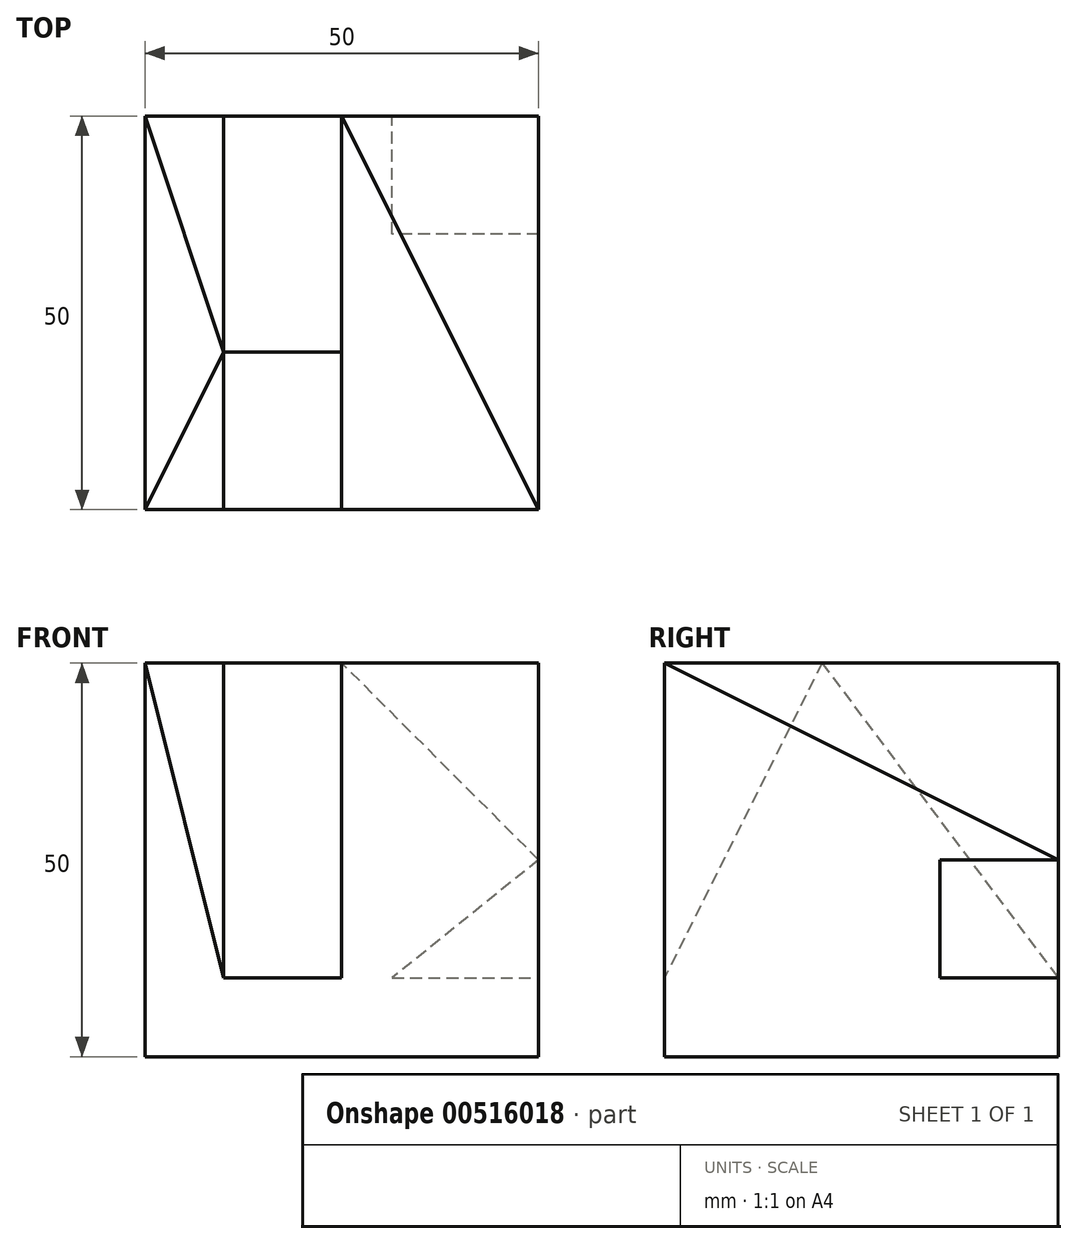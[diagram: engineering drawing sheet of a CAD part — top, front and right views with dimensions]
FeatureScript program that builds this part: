
annotation { "Feature Type Name" : "Feature", "Feature Type Description" : "" }
export const myFeature = defineFeature(function(context is Context, id is Id, definition is map)
    precondition{}
    {
        {
            var Q0;
            Q0=qCreatedBy(makeId("Top.planeOp"),FACE);
            var sketch = newSketch(context, id + "F0", { "sketchPlane" : qUnion([Q0])});
            skLineSegment(sketch, "E0.bottom", {"start": v(0, 0) * mm, "end": v(50, 0) * mm});
            skLineSegment(sketch, "E0.top", {"start": v(0, 50) * mm, "end": v(50, 50) * mm});
            skLineSegment(sketch, "E0.left", {"start": v(0, 0) * mm, "end": v(0, 50) * mm});
            skLineSegment(sketch, "E0.right", {"start": v(50, 0) * mm, "end": v(50, 50) * mm});
            skSolve(sketch);
        }
        {
            var Q0;
            Q0 = qSketchRegion(id + "F0", true);
            extrude(context, id + "F1", {"entities" : qUnion([Q0]), "depth" : 50 * mm, "offsetDistance" : 25 * mm});
        }
        {
            var Q0;
            Q0=makeQuery(id+"F1.opExtrude","SWEPT_FACE",FACE,{"disambiguationData":[OSD([sQuery(id+"F0.wireOp",EDGE,"E0.right")])]});
            var sketch = newSketch(context, id + "F2", { "sketchPlane" : qUnion([Q0])});
            skLineSegment(sketch, "E1.bottom", {"start": v(50, 25) * mm, "end": v(35, 25) * mm});
            skLineSegment(sketch, "E1.top", {"start": v(50, 10) * mm, "end": v(35, 10) * mm});
            skLineSegment(sketch, "E1.left", {"start": v(50, 25) * mm, "end": v(50, 10) * mm});
            skLineSegment(sketch, "E1.right", {"start": v(35, 25) * mm, "end": v(35, 10) * mm});
            skSolve(sketch);
        }
        {
            var Q0;
            Q0=makeQuery(id+"F1.opExtrude","CAP_FACE",FACE,{"disambiguationData":[OSD([sQuery(id+"F0.wireOp",EDGE,"E0.bottom"),sQuery(id+"F0.wireOp",EDGE,"E0.top"),sQuery(id+"F0.wireOp",EDGE,"E0.left"),sQuery(id+"F0.wireOp",EDGE,"E0.right")])],"isStart":false});
            var sketch = newSketch(context, id + "F3", { "sketchPlane" : qUnion([Q0])});
            skLineSegment(sketch, "E2", {"start": v(0, 50) * mm, "end": v(10, 20) * mm});
            skLineSegment(sketch, "E3", {"start": v(10, 20) * mm, "end": v(0, 0) * mm});
            skLineSegment(sketch, "E4", {"start": v(10, 20) * mm, "end": v(10, 0) * mm});
            skLineSegment(sketch, "E5", {"start": v(10, 0) * mm, "end": v(10, 50) * mm});
            skLineSegment(sketch, "E6", {"start": v(10, 20) * mm, "end": v(25, 20) * mm});
            skLineSegment(sketch, "E7", {"start": v(25, 20) * mm, "end": v(25, 50) * mm});
            skLineSegment(sketch, "E8", {"start": v(25, 50) * mm, "end": v(25, 0) * mm});
            skSolve(sketch);
        }
        {
            var Q0;
            Q0=makeQuery(id+"F1.opExtrude","SWEPT_FACE",FACE,{"disambiguationData":[OSD([sQuery(id+"F0.wireOp",EDGE,"E0.bottom")])]});
            var sketch = newSketch(context, id + "F4", { "sketchPlane" : qUnion([Q0])});
            skLineSegment(sketch, "E9", {"start": v(10, 50) * mm, "end": v(10, 14.74) * mm});
            skLineSegment(sketch, "E10", {"start": v(10, 14.74) * mm, "end": v(25, 14.74) * mm});
            skLineSegment(sketch, "E11", {"start": v(25, 14.74) * mm, "end": v(25, 50) * mm});
            skSolve(sketch);
        }
        {
            var Q0;
            Q0=makeQuery(id+"F1.opExtrude","SWEPT_FACE",FACE,{"disambiguationData":[OSD([sQuery(id+"F0.wireOp",EDGE,"E0.right")])]});
            var sketch = newSketch(context, id + "F5", { "sketchPlane" : qUnion([Q0])});
            skLineSegment(sketch, "E12", {"start": v(0, 10) * mm, "end": v(20, 50) * mm});
            skSolve(sketch);
        }
        {
            var Q0;
            {var subQ0=sQuery(id+"F3.wireOp",EDGE,"E6");Q0=makeQuery(id+"F3.imprint","IMPRINT",FACE,{"disambiguationData":[TD([[makeQuery(id+"F3.imprint","IMPRINT",EDGE,{"derivedFrom":subQ0}),-1.0]])]});}
            var Q1;
            {var subQ0=sQuery(id+"F4.wireOp",EDGE,"E9");Q1=makeQuery(id+"F4.imprint","IMPRINT",FACE,{"disambiguationData":[TD([[makeQuery(id+"F4.imprint","IMPRINT",EDGE,{"derivedFrom":subQ0}),1.0]])]});}
            var Q2;
            Q2=sQuery(id+"F5.wireOp",EDGE,"E12");
            sweep(context, id + "F6", {"operationType" : NewBodyOperationType.REMOVE, "profiles" : qUnion([Q0, Q1]), "path" : qUnion([Q2])});
        }
        {
            var Q0;
            Q0=makeQuery(id+"F1.opExtrude","SWEPT_FACE",FACE,{"disambiguationData":[OSD([sQuery(id+"F0.wireOp",EDGE,"E0.right")])]});
            var sketch = newSketch(context, id + "F7", { "sketchPlane" : qUnion([Q0])});
            skLineSegment(sketch, "E13", {"start": v(50, 10) * mm, "end": v(20, 50) * mm});
            skSolve(sketch);
        }
        {
            var Q0;
            {var subQ0=sQuery(id+"F3.wireOp",EDGE,"E6");Q0=makeQuery(id+"F3.imprint","IMPRINT",FACE,{"disambiguationData":[TD([[makeQuery(id+"F3.imprint","IMPRINT",EDGE,{"derivedFrom":subQ0}),1.0]])]});}
            var Q1;
            Q1=sQuery(id+"F7.wireOp",EDGE,"E13");
            sweep(context, id + "F8", {"operationType" : NewBodyOperationType.REMOVE, "profiles" : qUnion([Q0]), "path" : qUnion([Q1])});
        }
        {
            var Q0;
            {var subQ0=sQuery(id+"F3.wireOp",EDGE,"E3");Q0=makeQuery(id+"F3.imprint","IMPRINT",FACE,{"disambiguationData":[TD([[makeQuery(id+"F3.imprint","IMPRINT",EDGE,{"derivedFrom":subQ0}),1.0]])]});}
            var Q1;
            Q1=sQuery(id+"F5.wireOp",EDGE,"E12");
            sweep(context, id + "F9", {"operationType" : NewBodyOperationType.REMOVE, "profiles" : qUnion([Q0]), "path" : qUnion([Q1])});
        }
        {
            var Q0;
            {var subQ0=sQuery(id+"F3.wireOp",EDGE,"E2");Q0=makeQuery(id+"F3.imprint","IMPRINT",FACE,{"disambiguationData":[TD([[makeQuery(id+"F3.imprint","IMPRINT",EDGE,{"derivedFrom":subQ0}),1.0]])]});}
            var Q1;
            Q1=sQuery(id+"F7.wireOp",EDGE,"E13");
            sweep(context, id + "F10", {"operationType" : NewBodyOperationType.REMOVE, "profiles" : qUnion([Q0]), "path" : qUnion([Q1])});
        }
        {
            var Q0;
            {var subQ0=makeQuery(id+"F1.opExtrude","CAP_EDGE",EDGE,{"disambiguationData":[OSD([sQuery(id+"F0.wireOp",EDGE,"E0.right")])],"isStart":false});Q0=makeQuery(id+"F3.imprint","IMPRINT",FACE,{"disambiguationData":[TD([[makeQuery(id+"F3.imprint","IMPRINT",EDGE,{"derivedFrom":subQ0}),1.0]])]});}
            var sketch = newSketch(context, id + "F11", { "sketchPlane" : qUnion([Q0])});
            skLineSegment(sketch, "E14", {"start": v(25, 50) * mm, "end": v(50, 0) * mm});
            skSolve(sketch);
        }
        {
            var Q0;
            Q0=makeQuery(id+"F1.opExtrude","SWEPT_FACE",FACE,{"disambiguationData":[OSD([sQuery(id+"F0.wireOp",EDGE,"E0.right")])]});
            var sketch = newSketch(context, id + "F12", { "sketchPlane" : qUnion([Q0])});
            skLineSegment(sketch, "E15", {"start": v(0, 50) * mm, "end": v(50, 25) * mm});
            skSolve(sketch);
        }
        {
            var Q0;
            Q0=makeQuery(id+"F12.imprint","IMPRINT",FACE,{"disambiguationData":[TD([[makeQuery(id+"F12.imprint","IMPRINT",EDGE,{"derivedFrom":sQuery(id+"F12.wireOp",EDGE,"E15")}),1.0]])]});
            var Q1;
            Q1=sQuery(id+"F11.wireOp",EDGE,"E14");
            sweep(context, id + "F13", {"operationType" : NewBodyOperationType.REMOVE, "profiles" : qUnion([Q0]), "path" : qUnion([Q1])});
        }
        {
            var Q0;
            Q0=makeQuery(id+"F1.opExtrude","SWEPT_FACE",FACE,{"disambiguationData":[OSD([sQuery(id+"F0.wireOp",EDGE,"E0.top")])]});
            var sketch = newSketch(context, id + "F14", { "sketchPlane" : qUnion([Q0])});
            skLineSegment(sketch, "E16", {"start": v(-50, 25) * mm, "end": v(-31.4, 10) * mm});
            skLineSegment(sketch, "E17", {"start": v(-31.4, 10) * mm, "end": v(-50, 10) * mm});
            skSolve(sketch);
        }
        {
            var Q0;
            {var subQ0=sQuery(id+"F14.wireOp",EDGE,"E16");Q0=makeQuery(id+"F14.imprint","IMPRINT",FACE,{"disambiguationData":[TD([[makeQuery(id+"F14.imprint","IMPRINT",EDGE,{"derivedFrom":subQ0}),-1.0]])]});}
            extrude(context, id + "F15", {"entities" : qUnion([Q0]), "operationType" : NewBodyOperationType.REMOVE, "oppositeDirection" : true, "depth" : 15 * mm, "offsetDistance" : 25 * mm});
        }
    });
